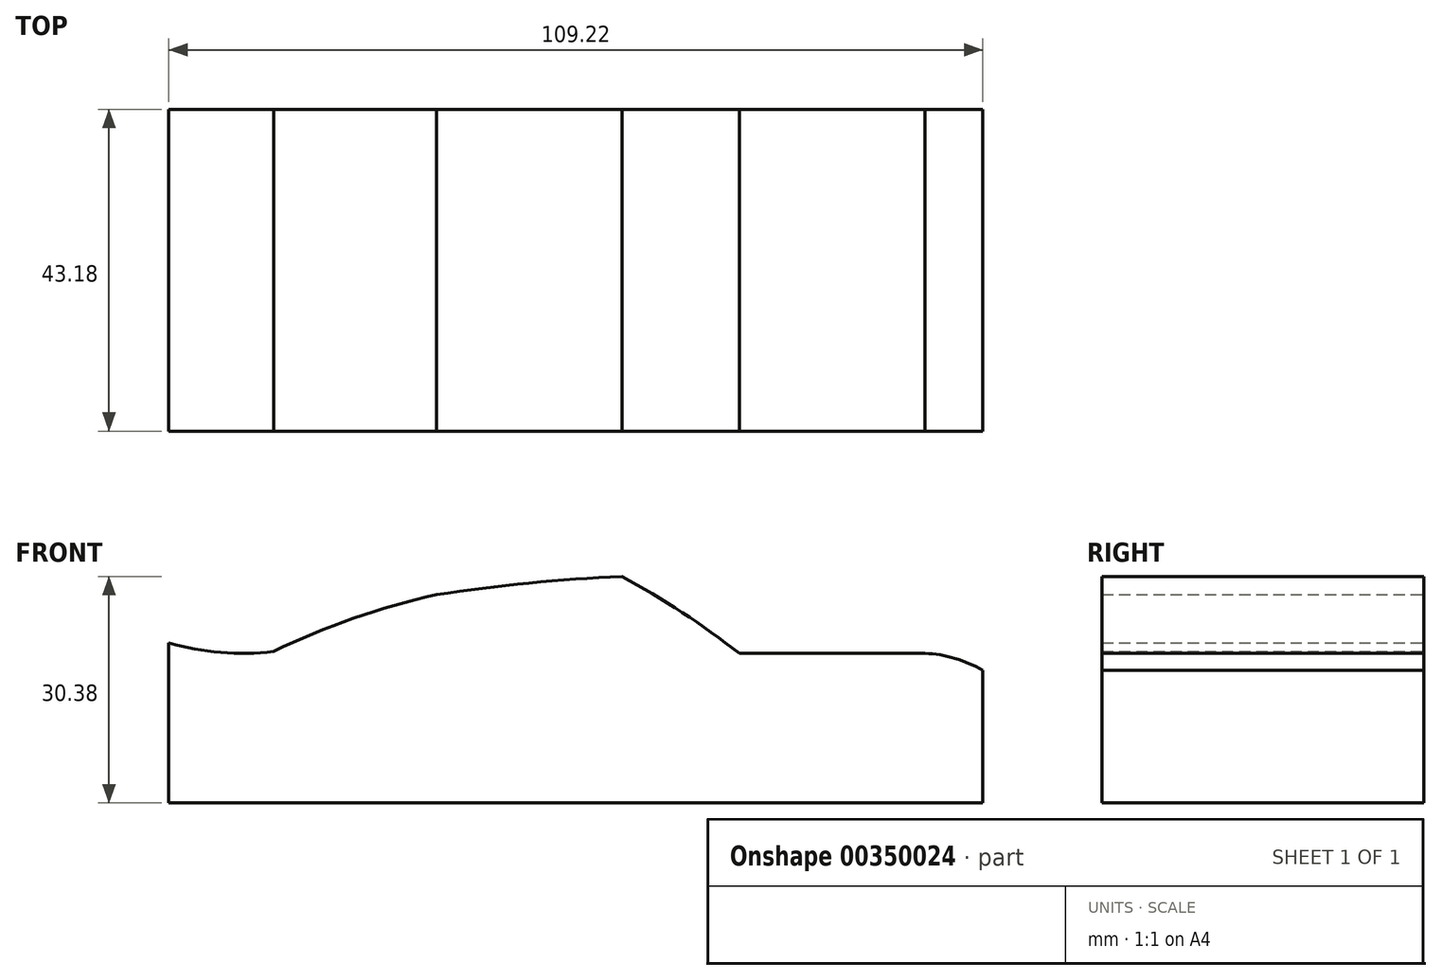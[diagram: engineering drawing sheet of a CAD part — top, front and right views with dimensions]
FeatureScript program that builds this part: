
annotation { "Feature Type Name" : "Feature", "Feature Type Description" : "" }
export const myFeature = defineFeature(function(context is Context, id is Id, definition is map)
    precondition{}
    {
        {
            var Q0;
            Q0=qCreatedBy(makeId("Front.planeOp"),FACE);
            var sketch = newSketch(context, id + "F0", { "sketchPlane" : qUnion([Q0])});
            skLineSegment(sketch, "E0.bottom", {"start": v(0, 0) * mm, "end": v(109.22, 0) * mm});
            skLineSegment(sketch, "E0.top", {"start": v(0, 30.48) * mm, "end": v(109.22, 30.48) * mm});
            skLineSegment(sketch, "E0.left", {"start": v(0, 0) * mm, "end": v(0, 30.48) * mm});
            skLineSegment(sketch, "E0.right", {"start": v(109.22, 0) * mm, "end": v(109.22, 30.48) * mm});
            skSolve(sketch);
        }
        {
            var Q0;
            Q0=makeQuery(id+"F0.imprint","IMPRINT",FACE,{"disambiguationData":[TD([[makeQuery(id+"F0.imprint","IMPRINT",EDGE,{"derivedFrom":sQuery(id+"F0.wireOp",EDGE,"E0.bottom")}),1.0]])]});
            extrude(context, id + "F1", {"entities" : qUnion([Q0]), "depth" : 43.18 * mm});
        }
        {
            var Q0;
            Q0=qCreatedBy(makeId("Front.planeOp"),FACE);
            var sketch = newSketch(context, id + "F2", { "sketchPlane" : qUnion([Q0])});
            skArc(sketch, "E1", {"start": v(109.22, 17.78) * mm, "mid": v(105.48, 19.4) * mm, "end": v(101.45, 20.07) * mm});
            skLineSegment(sketch, "E2", {"start": v(101.45, 20.07) * mm, "end": v(76.56, 20.07) * mm});
            skArc(sketch, "E3", {"start": v(76.56, 20.07) * mm, "mid": v(68.9, 25.56) * mm, "end": v(60.81, 30.38) * mm});
            skArc(sketch, "E4", {"start": v(60.81, 30.38) * mm, "mid": v(48.33, 29.5) * mm, "end": v(35.92, 27.94) * mm});
            skArc(sketch, "E5", {"start": v(35.92, 27.94) * mm, "mid": v(24.77, 24.77) * mm, "end": v(14.07, 20.32) * mm});
            skArc(sketch, "E6", {"start": v(0, 21.48) * mm, "mid": v(6.98, 20.18) * mm, "end": v(14.07, 20.32) * mm});
            skLineSegment(sketch, "E7", {"start": v(109.22, 17.78) * mm, "end": v(109.22, 32.64) * mm});
            skLineSegment(sketch, "E8", {"start": v(109.22, 32.64) * mm, "end": v(0, 32.64) * mm});
            skLineSegment(sketch, "E9", {"start": v(0, 32.64) * mm, "end": v(0, 21.48) * mm});
            skSolve(sketch);
        }
        {
            var Q0;
            Q0=makeQuery(id+"F2.imprint","IMPRINT",FACE,{"disambiguationData":[TD([[makeQuery(id+"F2.imprint","IMPRINT",EDGE,{"derivedFrom":sQuery(id+"F2.wireOp",EDGE,"E1")}),-1.0]])]});
            extrude(context, id + "F3", {"entities" : qUnion([Q0]), "operationType" : NewBodyOperationType.REMOVE, "endBound" : BoundingType.THROUGH_ALL, "depth" : 25.4 * mm});
        }
    });
